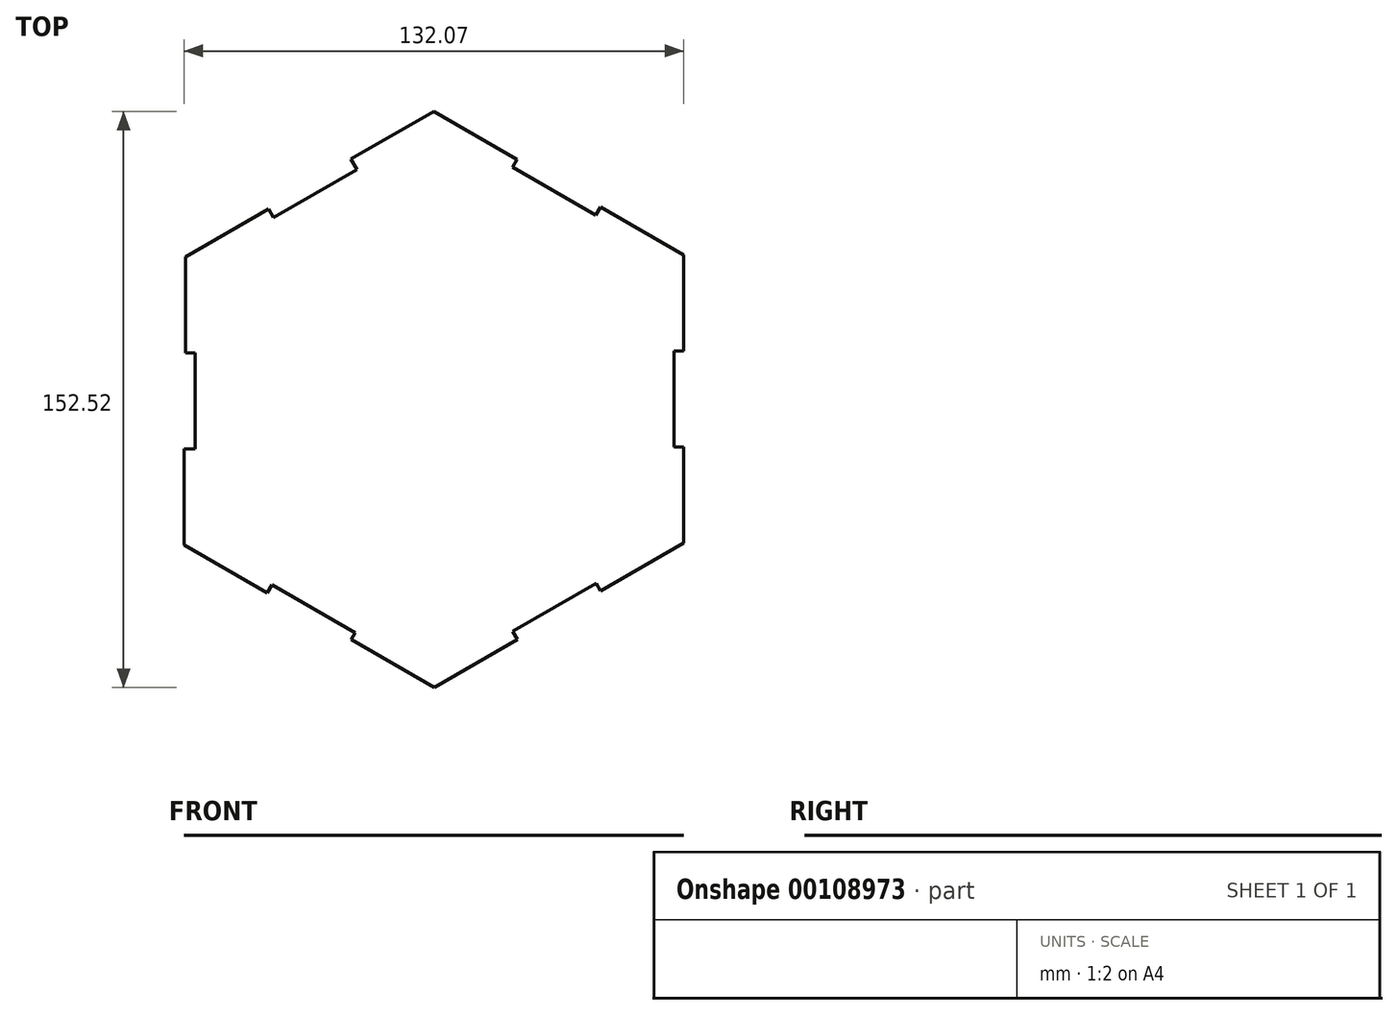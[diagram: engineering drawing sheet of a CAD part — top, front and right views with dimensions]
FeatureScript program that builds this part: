
annotation { "Feature Type Name" : "Feature", "Feature Type Description" : "" }
export const myFeature = defineFeature(function(context is Context, id is Id, definition is map)
    precondition{}
    {
        {
            var Q0;
            Q0=qCreatedBy(makeId("Top.planeOp"),FACE);
            var sketch = newSketch(context, id + "F0", { "sketchPlane" : qUnion([Q0])});
            skLineSegment(sketch, "E0", {"start": v(-65.67, 37.55) * mm, "end": v(-65.67, 12.15) * mm});
            skLineSegment(sketch, "E1", {"start": v(-66.03, -38.65) * mm, "end": v(-66.03, -13.25) * mm});
            skLineSegment(sketch, "E2", {"start": v(-65.67, 12.15) * mm, "end": v(-63.13, 12.15) * mm});
            skLineSegment(sketch, "E3", {"start": v(-63.13, 12.15) * mm, "end": v(-63.13, -13.25) * mm});
            skLineSegment(sketch, "E4", {"start": v(-63.13, -13.25) * mm, "end": v(-66.03, -13.25) * mm});
            skLineSegment(sketch, "E5", {"start": v(-65.67, 37.55) * mm, "end": v(-43.66, 50.21) * mm});
            skLineSegment(sketch, "E6", {"start": v(0, 76.1) * mm, "end": v(-22.01, 63.44) * mm});
            skLineSegment(sketch, "E7", {"start": v(-43.66, 50.21) * mm, "end": v(-42.4, 48.01) * mm});
            skLineSegment(sketch, "E8", {"start": v(-42.4, 48.01) * mm, "end": v(-20.37, 60.68) * mm});
            skLineSegment(sketch, "E9", {"start": v(-20.37, 60.68) * mm, "end": v(-22.01, 63.44) * mm});
            skLineSegment(sketch, "E10", {"start": v(0, 76.1) * mm, "end": v(22, 63.4) * mm});
            skLineSegment(sketch, "E11", {"start": v(22, 63.4) * mm, "end": v(20.77, 61.26) * mm});
            skLineSegment(sketch, "E12", {"start": v(20.77, 61.26) * mm, "end": v(42.76, 48.56) * mm});
            skLineSegment(sketch, "E13", {"start": v(42.76, 48.56) * mm, "end": v(44.03, 50.76) * mm});
            skLineSegment(sketch, "E14", {"start": v(44.03, 50.76) * mm, "end": v(66.03, 38.06) * mm});
            skLineSegment(sketch, "E15", {"start": v(66.03, 38.06) * mm, "end": v(66.03, 12.66) * mm});
            skLineSegment(sketch, "E16", {"start": v(66.03, 12.66) * mm, "end": v(63.5, 12.66) * mm});
            skLineSegment(sketch, "E17", {"start": v(63.5, 12.66) * mm, "end": v(63.5, -12.74) * mm});
            skLineSegment(sketch, "E18", {"start": v(63.5, -12.74) * mm, "end": v(66.04, -12.74) * mm});
            skLineSegment(sketch, "E19", {"start": v(66.04, -12.74) * mm, "end": v(66.04, -38.14) * mm});
            skLineSegment(sketch, "E20", {"start": v(66.04, -38.14) * mm, "end": v(44.04, -50.84) * mm});
            skLineSegment(sketch, "E21", {"start": v(44.04, -50.84) * mm, "end": v(42.88, -48.82) * mm});
            skLineSegment(sketch, "E22", {"start": v(42.88, -48.82) * mm, "end": v(20.88, -61.52) * mm});
            skLineSegment(sketch, "E23", {"start": v(20.88, -61.52) * mm, "end": v(22.15, -63.72) * mm});
            skLineSegment(sketch, "E24", {"start": v(22.15, -63.72) * mm, "end": v(0.15, -76.42) * mm});
            skLineSegment(sketch, "E25", {"start": v(0.15, -76.42) * mm, "end": v(-21.84, -63.72) * mm});
            skLineSegment(sketch, "E26", {"start": v(-21.84, -63.72) * mm, "end": v(-20.77, -61.85) * mm});
            skLineSegment(sketch, "E27", {"start": v(-20.77, -61.85) * mm, "end": v(-42.76, -49.15) * mm});
            skLineSegment(sketch, "E28", {"start": v(-42.76, -49.15) * mm, "end": v(-44.03, -51.35) * mm});
            skLineSegment(sketch, "E29", {"start": v(-44.03, -51.35) * mm, "end": v(-66.03, -38.65) * mm});
            skSolve(sketch);
        }
        {
            var Q0;
            Q0=makeQuery(id+"F0.imprint","IMPRINT",FACE,{"disambiguationData":[TD([[makeQuery(id+"F0.imprint","IMPRINT",EDGE,{"derivedFrom":sQuery(id+"F0.wireOp",EDGE,"E0")}),1.0]])]});
            extrude(context, id + "F1", {"entities" : qUnion([Q0]), "depth" : 1 / 203.2 * mm});
        }
    });
